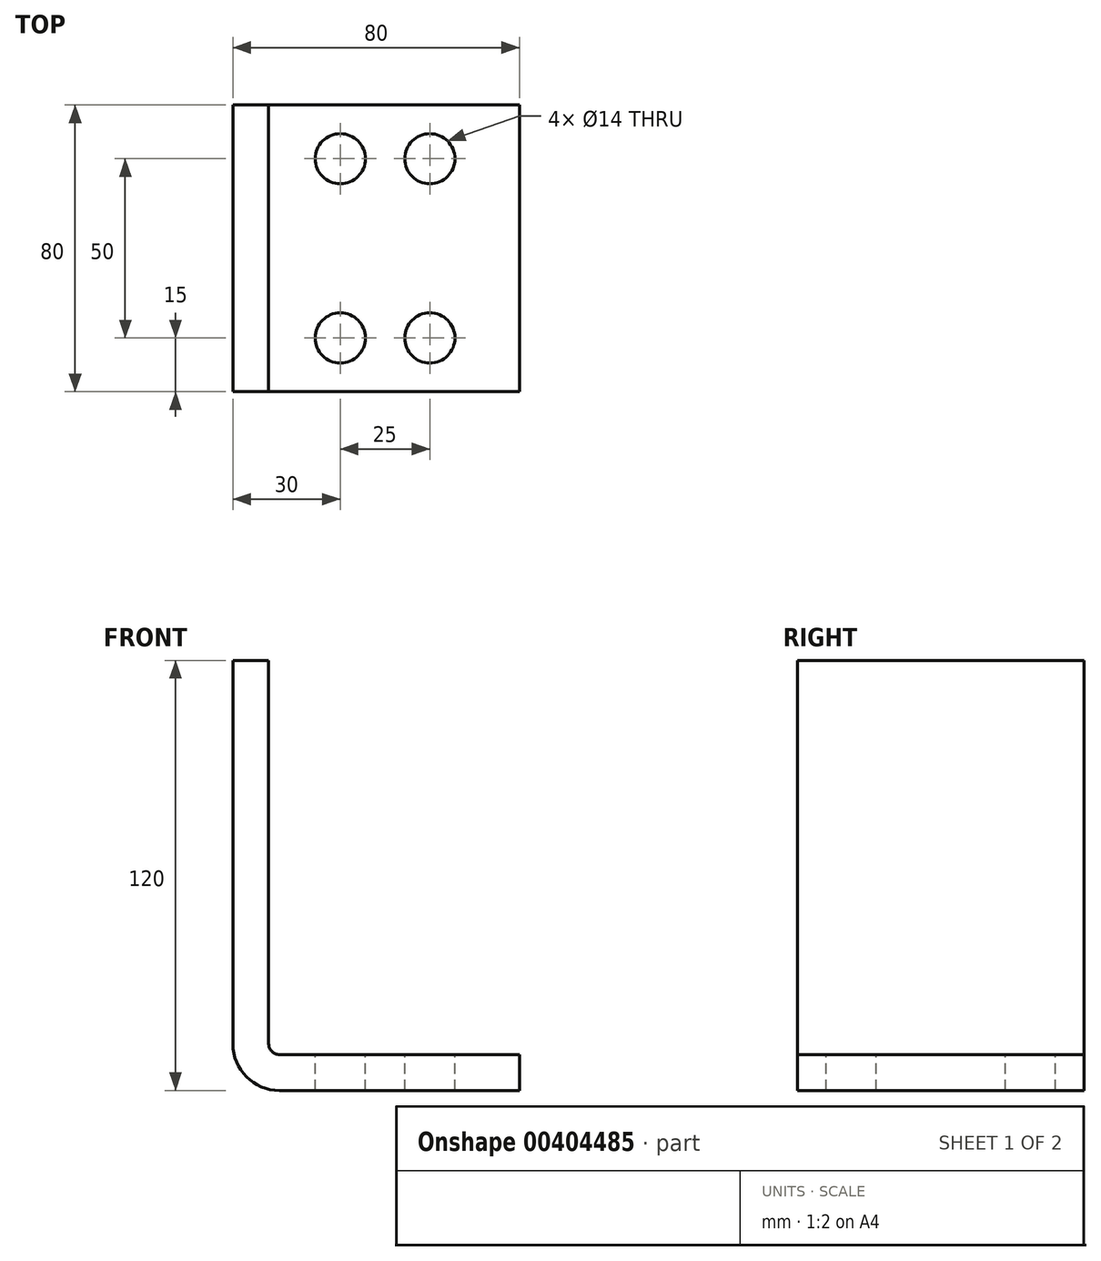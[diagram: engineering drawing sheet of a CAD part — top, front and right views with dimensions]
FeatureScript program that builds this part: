
annotation { "Feature Type Name" : "Feature", "Feature Type Description" : "" }
export const myFeature = defineFeature(function(context is Context, id is Id, definition is map)
    precondition{}
    {
        {
            var Q0;
            Q0=qCreatedBy(makeId("Front.planeOp"),FACE);
            var sketch = newSketch(context, id + "F0", { "sketchPlane" : qUnion([Q0])});
            skLineSegment(sketch, "E0", {"start": v(0, 120) * mm, "end": v(0, 0) * mm});
            skLineSegment(sketch, "E1", {"start": v(0, 0) * mm, "end": v(80, 0) * mm});
            skLineSegment(sketch, "E2.0", {"start": v(10, 10) * mm, "end": v(80, 10) * mm});
            skLineSegment(sketch, "E2.1", {"start": v(10, 120) * mm, "end": v(10, 10) * mm});
            skLineSegment(sketch, "E3", {"start": v(80, 0) * mm, "end": v(80, 10) * mm});
            skLineSegment(sketch, "E4", {"start": v(0, 120) * mm, "end": v(10, 120) * mm});
            skSolve(sketch);
        }
        {
            var Q0;
            Q0 = qSketchRegion(id + "F0", true);
            extrude(context, id + "F1", {"entities" : qUnion([Q0]), "endBound" : BoundingType.SYMMETRIC, "oppositeDirection" : true, "depth" : 80 * mm});
        }
        {
            var Q0;
            Q0=makeQuery(id+"F1.opExtrude","SWEPT_EDGE",EDGE,{"disambiguationData":[OSD([sQuery(id+"F0.wireOp",EDGE,"E2.0"),sQuery(id+"F0.wireOp",EDGE,"E2.1")])]});
            fillet(context, id + "F2", {"entities" : qUnion([Q0]), "radius" : 3 * mm, "tangentPropagation" : true, "allowEdgeOverflow" : false});
        }
        {
            var Q0;
            Q0=makeQuery(id+"F1.opExtrude","SWEPT_EDGE",EDGE,{"disambiguationData":[OSD([sQuery(id+"F0.wireOp",EDGE,"E0"),sQuery(id+"F0.wireOp",EDGE,"E1")])]});
            fillet(context, id + "F3", {"entities" : qUnion([Q0]), "radius" : 13 * mm, "tangentPropagation" : true, "allowEdgeOverflow" : false});
        }
        {
            var Q0;
            Q0=makeQuery(id+"F1.opExtrude","SWEPT_FACE",FACE,{"disambiguationData":[OSD([sQuery(id+"F0.wireOp",EDGE,"E2.0")])]});
            var sketch = newSketch(context, id + "F4", { "sketchPlane" : qUnion([Q0])});
            skLineSegment(sketch, "E5", {"start": v(80, 0) * mm, "end": v(13, 0) * mm, "construction": true});
            skPoint(sketch, "E6", {"position": v(55, 25) * mm});
            skPoint(sketch, "E7", {"position": v(30, 25) * mm});
            skPoint(sketch, "E8.MirrorP", {"position": v(55, -25) * mm});
            skPoint(sketch, "E9.MirrorP", {"position": v(30, -25) * mm});
            skSolve(sketch);
        }
        {
            var Q0;
            Q0=sQuery(id+"F4.wireOp",VERTEX,"E6");
            var Q1;
            Q1=sQuery(id+"F4.wireOp",VERTEX,"E8.MirrorP");
            var Q2;
            Q2=sQuery(id+"F4.wireOp",VERTEX,"E9.MirrorP");
            var Q3;
            Q3=sQuery(id+"F4.wireOp",VERTEX,"E7");
            var Q4;
            Q4=makeQuery(id+"F1.opExtrude","SWEPT_BODY",BODY,{"disambiguationData":[OSD([sQuery(id+"F0.wireOp",EDGE,"E0"),sQuery(id+"F0.wireOp",EDGE,"E1"),sQuery(id+"F0.wireOp",EDGE,"E2.0"),sQuery(id+"F0.wireOp",EDGE,"E2.1"),sQuery(id+"F0.wireOp",EDGE,"E3"),sQuery(id+"F0.wireOp",EDGE,"E4")])]});
            hole(context, id + "F5", {"style" : HoleStyle.SIMPLE, "endStyle" : HoleEndStyle.THROUGH, "standardTappedOrClearance" : lookupTablePath({ "fit" : "Normal", "standard" : "ISO", "size" : "14", "type" : "Drilled" }), "standardBlindInLast" : lookupTablePath({ "fit" : "Standard", "standard" : "ISO", "size" : "14", "type" : "Drilled" }), "holeDiameter" : 14 * mm, "isTappedThrough" : true, "tappedDepth" : 12 * mm, "tapClearance" : 3, "locations" : qUnion([Q0, Q1, Q2, Q3]), "scope" : qUnion([Q4])});
        }
    });
